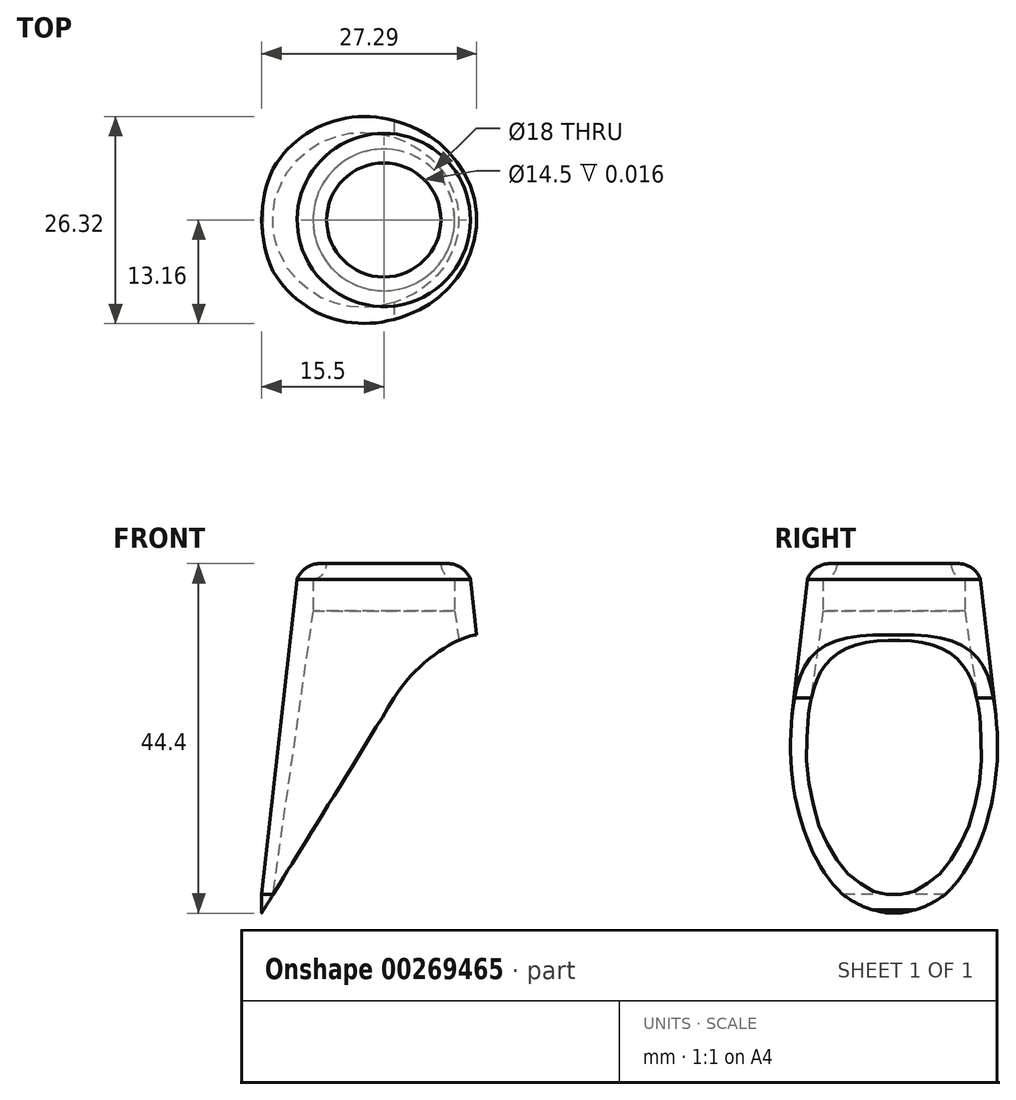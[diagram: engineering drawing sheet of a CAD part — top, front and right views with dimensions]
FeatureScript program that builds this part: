
annotation { "Feature Type Name" : "Feature", "Feature Type Description" : "" }
export const myFeature = defineFeature(function(context is Context, id is Id, definition is map)
    precondition{}
    {
        {
            var Q0;
            Q0=qCreatedBy(makeId("Top.planeOp"),FACE);
            var sketch = newSketch(context, id + "F0", { "sketchPlane" : qUnion([Q0])});
            skCircle(sketch, "E0", {"center": v(0, 0) * mm, "radius": 9 * mm});
            skCircle(sketch, "E1", {"center": v(0, 0) * mm, "radius": 15.5 * mm});
            skLineSegment(sketch, "E2", {"start": v(-16.2, -40) * mm, "end": v(-16.2, 50.82) * mm, "construction": true});
            skSolve(sketch);
        }
        {
            var Q0;
            Q0=makeQuery(id+"F0.imprint","IMPRINT",FACE,{"disambiguationData":[TD([[makeQuery(id+"F0.imprint","IMPRINT",EDGE,{"derivedFrom":sQuery(id+"F0.wireOp",EDGE,"E0")}),-1.0]])]});
            extrude(context, id + "F1", {"entities" : qUnion([Q0]), "depth" : 41 * mm, "hasSecondDirection" : true, "secondDirectionOppositeDirection" : true, "secondDirectionDepth" : 5 * mm});
        }
        {
            var Q0;
            Q0=makeQuery(id+"F1.opExtrude","CAP_EDGE",EDGE,{"disambiguationData":[OSD([sQuery(id+"F0.wireOp",EDGE,"E1")])],"isStart":false});
            chamfer(context, id + "F2", {"entities" : qUnion([Q0]), "chamferType" : ChamferType.TWO_OFFSETS, "width1" : 4.5 * mm, "oppositeDirection" : false, "width2" : 40 * mm, "tangentPropagation" : true});
        }
        {
            var Q0;
            Q0=makeQuery(id+"F1.opExtrude","CAP_EDGE",EDGE,{"disambiguationData":[OSD([sQuery(id+"F0.wireOp",EDGE,"E0")])],"isStart":true});
            chamfer(context, id + "F3", {"entities" : qUnion([Q0]), "chamferType" : ChamferType.TWO_OFFSETS, "width1" : 6 * mm, "oppositeDirection" : false, "width2" : 42 * mm, "tangentPropagation" : true});
        }
        {
            var Q0;
            Q0=qCreatedBy(makeId("Front.planeOp"),FACE);
            var sketch = newSketch(context, id + "F4", { "sketchPlane" : qUnion([Q0])});
            skLineSegment(sketch, "E3", {"start": v(-15.29, -1) * mm, "end": v(1.32, 25.93) * mm});
            skFitSpline(sketch, "E4", {"points": [v(1.32, 25.93) * mm, v(11.4, 33.9) * mm, v(17.65, 29.65) * mm, v(18.49, -10.38) * mm, v(-15.43, -10.46) * mm, v(-15.29, -1) * mm], "startDerivative": vector(40.5, 69.06) * mm, "endDerivative": vector(31.3, 55.59) * mm});
            skSolve(sketch);
        }
        {
            var Q0;
            Q0=makeQuery(id+"F4.imprint","IMPRINT",FACE,{"disambiguationData":[TD([[makeQuery(id+"F4.imprint","IMPRINT",EDGE,{"derivedFrom":sQuery(id+"F4.wireOp",EDGE,"E3")}),-1.0]])]});
            extrude(context, id + "F5", {"entities" : qUnion([Q0]), "operationType" : NewBodyOperationType.REMOVE, "endBound" : BoundingType.SYMMETRIC, "oppositeDirection" : true, "depth" : 37.2 * mm});
        }
        {
            var Q0;
            Q0=makeQuery(id+"F1.opExtrude","CAP_FACE",FACE,{"disambiguationData":[OSD([sQuery(id+"F0.wireOp",EDGE,"E0"),sQuery(id+"F0.wireOp",EDGE,"E1")])],"isStart":false});
            var sketch = newSketch(context, id + "F6", { "sketchPlane" : qUnion([Q0])});
            skCircle(sketch, "E5", {"center": v(0, 0) * mm, "radius": 7.25 * mm});
            skCircle(sketch, "E6", {"center": v(0, 0) * mm, "radius": 9.02 * mm});
            skSolve(sketch);
        }
        {
            var Q0;
            Q0=makeQuery(id+"F6.imprint","IMPRINT",FACE,{"disambiguationData":[TD([[makeQuery(id+"F6.imprint","IMPRINT",EDGE,{"derivedFrom":sQuery(id+"F6.wireOp",EDGE,"E5")}),-1.0]])]});
            var Q1;
            Q1=makeQuery(id+"F6.imprint","IMPRINT",FACE,{"disambiguationData":[TD([[makeQuery(id+"F6.imprint","IMPRINT",EDGE,{"derivedFrom":sQuery(id+"F6.wireOp",EDGE,"E6")}),1.0]])]});
            var Q2;
            Q2=makeQuery(id+"F6.imprint","IMPRINT",FACE,{"disambiguationData":[TD([[makeQuery(id+"F6.imprint","IMPRINT",EDGE,{"derivedFrom":sQuery(id+"F6.wireOp",EDGE,"E6")}),-1.0]])]});
            var Q3;
            {var subQ0=sQuery(id+"F0.wireOp",EDGE,"E1");var subQ1=sQuery(id+"F0.wireOp",EDGE,"E0");var subQ2=makeQuery(id+"F1.opExtrude","CAP_FACE",FACE,{"disambiguationData":[OSD([subQ1,subQ0])],"isStart":false});Q3=makeQuery(id+"F6.imprint","IMPRINT",FACE,{"disambiguationData":[TD([[makeQuery(id+"F6.imprint","IMPRINT",EDGE,{"derivedFrom":makeQuery(id+"F2.opChamfer","BLEND_EDGE",EDGE,{"blendedFrom":[makeQuery(id+"F1.opExtrude","CAP_EDGE",EDGE,{"disambiguationData":[OSD([subQ0])],"isStart":false}),subQ2],"blendedInto":[subQ2]})}),1.0]])]});}
            extrude(context, id + "F7", {"entities" : qUnion([Q0, Q1, Q2, Q3]), "operationType" : NewBodyOperationType.ADD, "depth" : 2 * mm});
        }
        {
            var Q0;
            Q0=makeQuery(id+"F7.opExtrude","CAP_EDGE",EDGE,{"disambiguationData":[OSD([sQuery(id+"F0.wireOp",EDGE,"E0"),sQuery(id+"F0.wireOp",EDGE,"E1")])],"isStart":false});
            fillet(context, id + "F8", {"entities" : qUnion([Q0]), "radius" : 3 * mm, "tangentPropagation" : true, "allowEdgeOverflow" : false});
        }
        {
            var Q0;
            Q0=makeQuery(id+"F7.opExtrude","CAP_EDGE",EDGE,{"disambiguationData":[OSD([sQuery(id+"F6.wireOp",EDGE,"E5")])],"isStart":true});
            fillet(context, id + "F9", {"entities" : qUnion([Q0]), "radius" : 2 * mm, "tangentPropagation" : true, "allowEdgeOverflow" : false});
        }
    });
